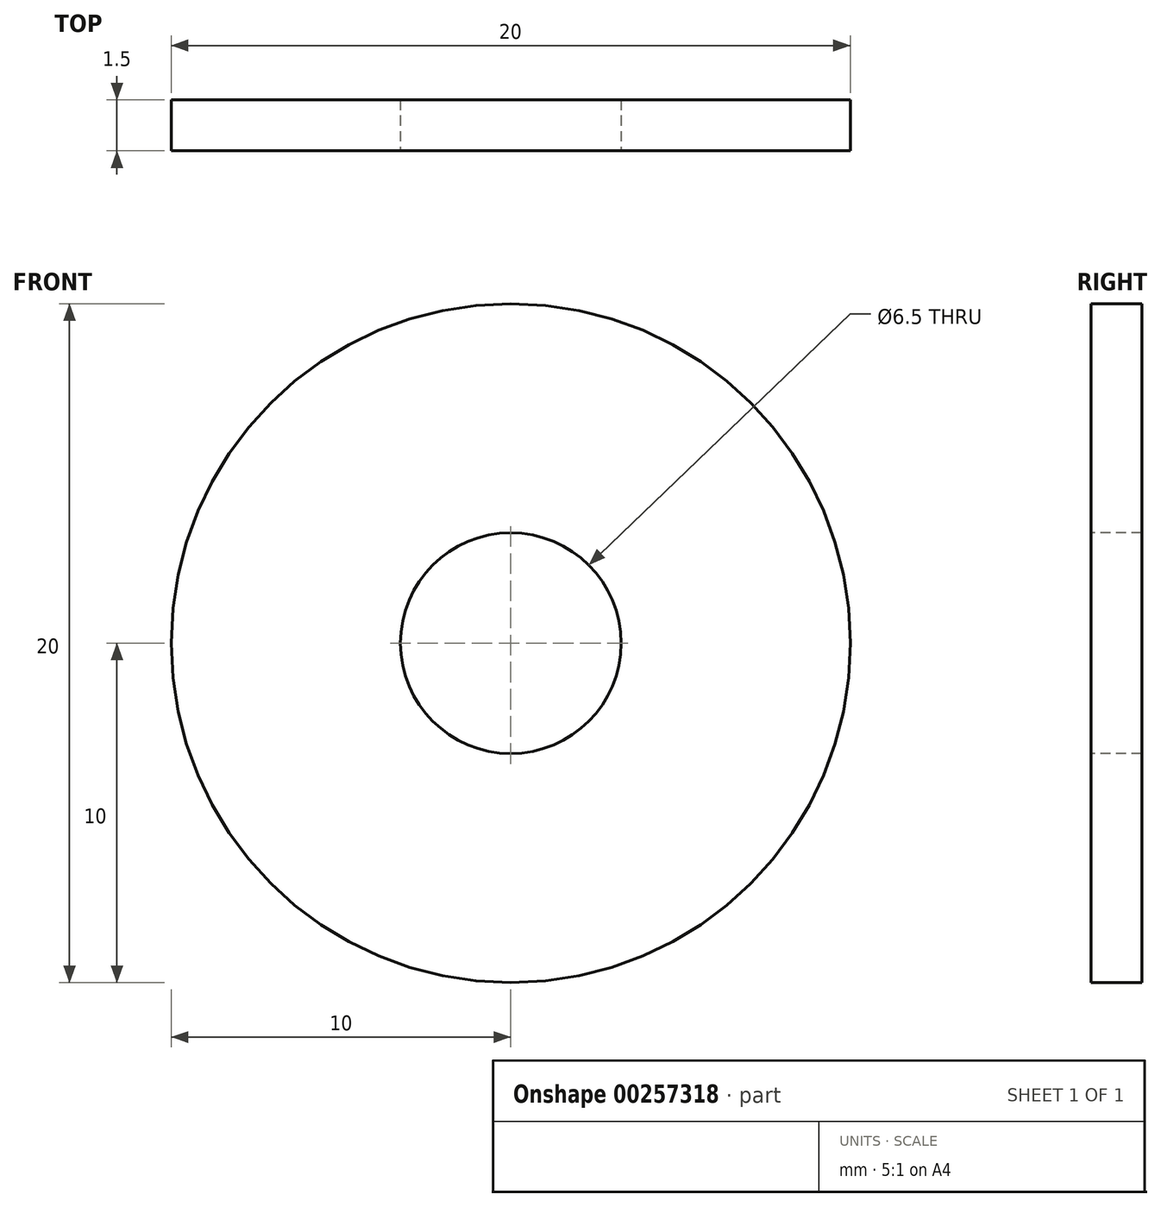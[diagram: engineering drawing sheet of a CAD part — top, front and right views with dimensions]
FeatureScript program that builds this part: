
annotation { "Feature Type Name" : "Feature", "Feature Type Description" : "" }
export const myFeature = defineFeature(function(context is Context, id is Id, definition is map)
    precondition{}
    {
        {
            var Q0;
            Q0=qCreatedBy(makeId("Front.planeOp"),FACE);
            var sketch = newSketch(context, id + "F0", { "sketchPlane" : qUnion([Q0])});
            skCircle(sketch, "E0", {"center": v(0, 0) * mm, "radius": 10 * mm});
            skSolve(sketch);
        }
        {
            var Q0;
            Q0=makeQuery(id+"F0.imprint","IMPRINT",FACE,{"disambiguationData":[TD([[makeQuery(id+"F0.imprint","IMPRINT",EDGE,{"derivedFrom":sQuery(id+"F0.wireOp",EDGE,"E0")}),1.0]])]});
            extrude(context, id + "F1", {"entities" : qUnion([Q0]), "oppositeDirection" : true, "depth" : 1.5 * mm});
        }
        {
            var Q0;
            Q0=sQuery(id+"F0.wireOp",VERTEX,"E0.center");
            var Q1;
            Q1=makeQuery(id+"F1.opExtrude","SWEPT_BODY",BODY,{"disambiguationData":[OSD([sQuery(id+"F0.wireOp",EDGE,"E0")])]});
            hole(context, id + "F2", {"style" : HoleStyle.SIMPLE, "endStyle" : HoleEndStyle.THROUGH, "holeDiameter" : 6.5 * mm, "tappedDepth" : 12 * mm, "tapClearance" : 3, "locations" : qUnion([Q0]), "scope" : qUnion([Q1])});
        }
    });
